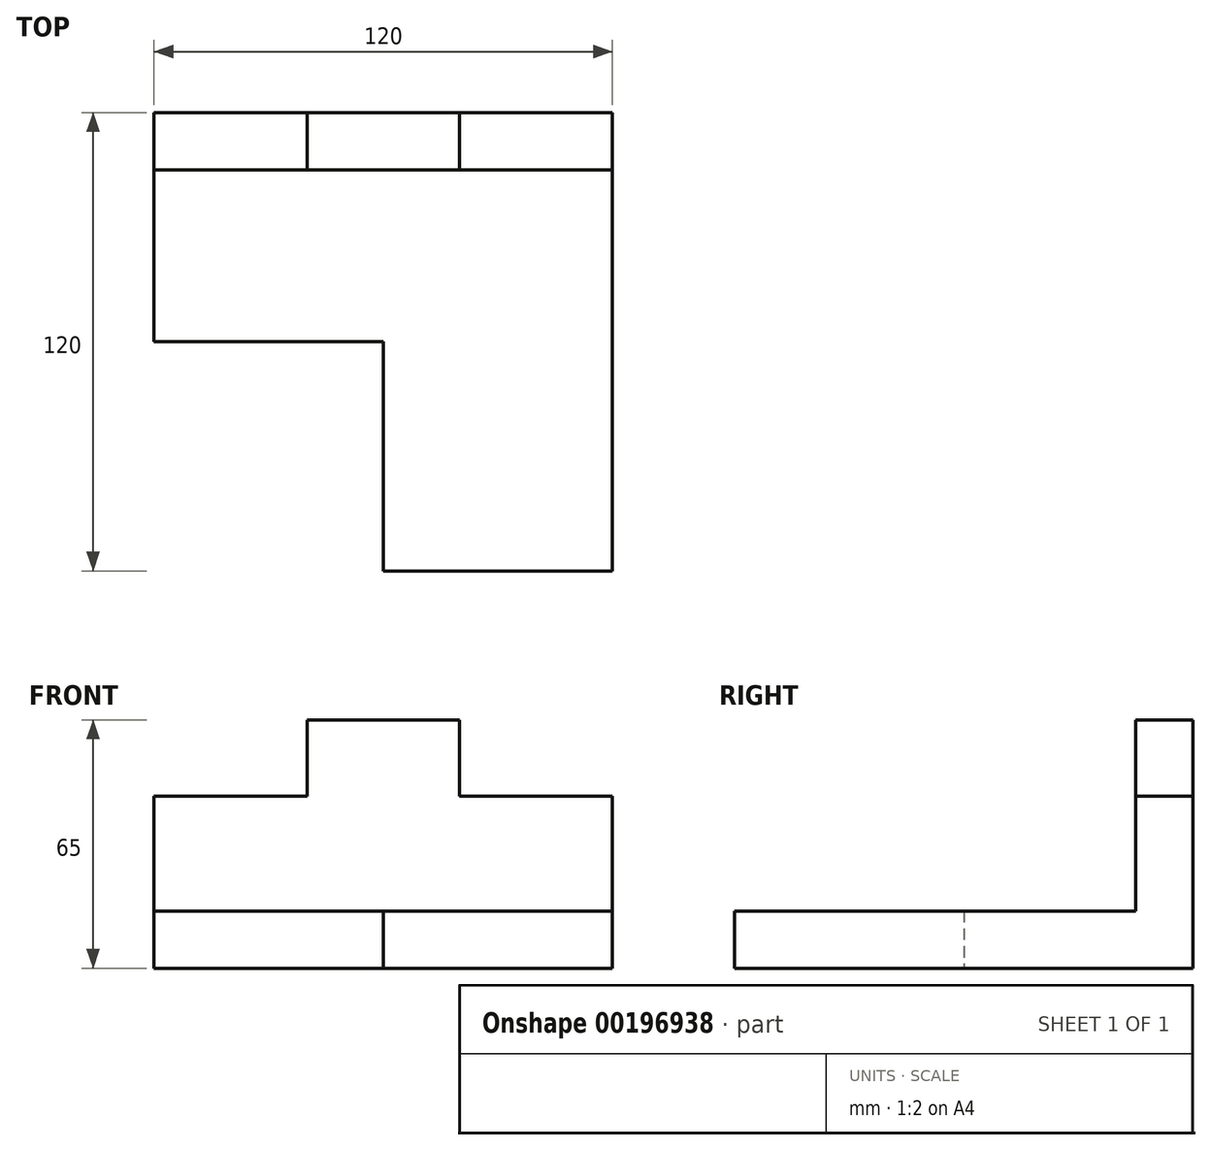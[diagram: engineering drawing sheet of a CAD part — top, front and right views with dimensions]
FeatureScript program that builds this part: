
annotation { "Feature Type Name" : "Feature", "Feature Type Description" : "" }
export const myFeature = defineFeature(function(context is Context, id is Id, definition is map)
    precondition{}
    {
        {
            var Q0;
            Q0=qCreatedBy(makeId("Front.planeOp"),FACE);
            var sketch = newSketch(context, id + "F0", { "sketchPlane" : qUnion([Q0])});
            skLineSegment(sketch, "E0", {"start": v(0, 0) * mm, "end": v(120, 0) * mm});
            skLineSegment(sketch, "E1", {"start": v(120, 0) * mm, "end": v(120, 45) * mm});
            skLineSegment(sketch, "E2", {"start": v(120, 45) * mm, "end": v(80, 45) * mm});
            skLineSegment(sketch, "E3", {"start": v(80, 45) * mm, "end": v(80, 65) * mm});
            skLineSegment(sketch, "E4", {"start": v(80, 65) * mm, "end": v(40, 65) * mm});
            skLineSegment(sketch, "E5", {"start": v(40, 65) * mm, "end": v(40, 45) * mm});
            skLineSegment(sketch, "E6", {"start": v(40, 45) * mm, "end": v(0, 45) * mm});
            skLineSegment(sketch, "E7", {"start": v(0, 45) * mm, "end": v(0, 0) * mm});
            skLineSegment(sketch, "E8", {"start": v(0, 15) * mm, "end": v(120, 15) * mm});
            skSolve(sketch);
        }
        {
            var Q0;
            {var subQ0=sQuery(id+"F0.wireOp",EDGE,"E2");Q0=makeQuery(id+"F0.imprint","IMPRINT",FACE,{"disambiguationData":[TD([[makeQuery(id+"F0.imprint","IMPRINT",EDGE,{"derivedFrom":subQ0}),1.0]])]});}
            var Q1;
            {var subQ0=sQuery(id+"F0.wireOp",EDGE,"E0");Q1=makeQuery(id+"F0.imprint","IMPRINT",FACE,{"disambiguationData":[TD([[makeQuery(id+"F0.imprint","IMPRINT",EDGE,{"derivedFrom":subQ0}),1.0]])]});}
            extrude(context, id + "F1", {"entities" : qUnion([Q0, Q1]), "depth" : 15 * mm});
        }
        {
            var Q0;
            Q0=makeQuery(id+"F1.opExtrude","SWEPT_FACE",FACE,{"disambiguationData":[OSD([sQuery(id+"F0.wireOp",EDGE,"E0")])]});
            var sketch = newSketch(context, id + "F2", { "sketchPlane" : qUnion([Q0])});
            skLineSegment(sketch, "E9.bottom", {"start": v(0, 0) * mm, "end": v(120, 0) * mm});
            skLineSegment(sketch, "E9.top", {"start": v(0, 120) * mm, "end": v(120, 120) * mm});
            skLineSegment(sketch, "E9.left", {"start": v(0, 0) * mm, "end": v(0, 120) * mm});
            skLineSegment(sketch, "E9.right", {"start": v(120, 0) * mm, "end": v(120, 120) * mm});
            skLineSegment(sketch, "E10", {"start": v(0, 60) * mm, "end": v(60, 60) * mm});
            skPoint(sketch, "E10.endSnap0", {"position": v(60, 120) * mm});
            skLineSegment(sketch, "E11", {"start": v(60, 60) * mm, "end": v(60, 120) * mm});
            skSolve(sketch);
        }
        {
            var Q0;
            {var subQ0=sQuery(id+"F2.wireOp",EDGE,"E9.bottom");Q0=makeQuery(id+"F2.imprint","IMPRINT",FACE,{"disambiguationData":[TD([[makeQuery(id+"F2.imprint","IMPRINT",EDGE,{"derivedFrom":subQ0}),1.0]])]});}
            var Q1;
            {var subQ4=sQuery(id+"F2.wireOp",EDGE,"E10");Q1=makeQuery(id+"F2.imprint","IMPRINT",FACE,{"disambiguationData":[TD([[makeQuery(id+"F2.imprint","IMPRINT",EDGE,{"derivedFrom":subQ4}),-1.0]])]});}
            extrude(context, id + "F3", {"entities" : qUnion([Q0, Q1]), "operationType" : NewBodyOperationType.ADD, "oppositeDirection" : true, "depth" : 15 * mm});
        }
    });
